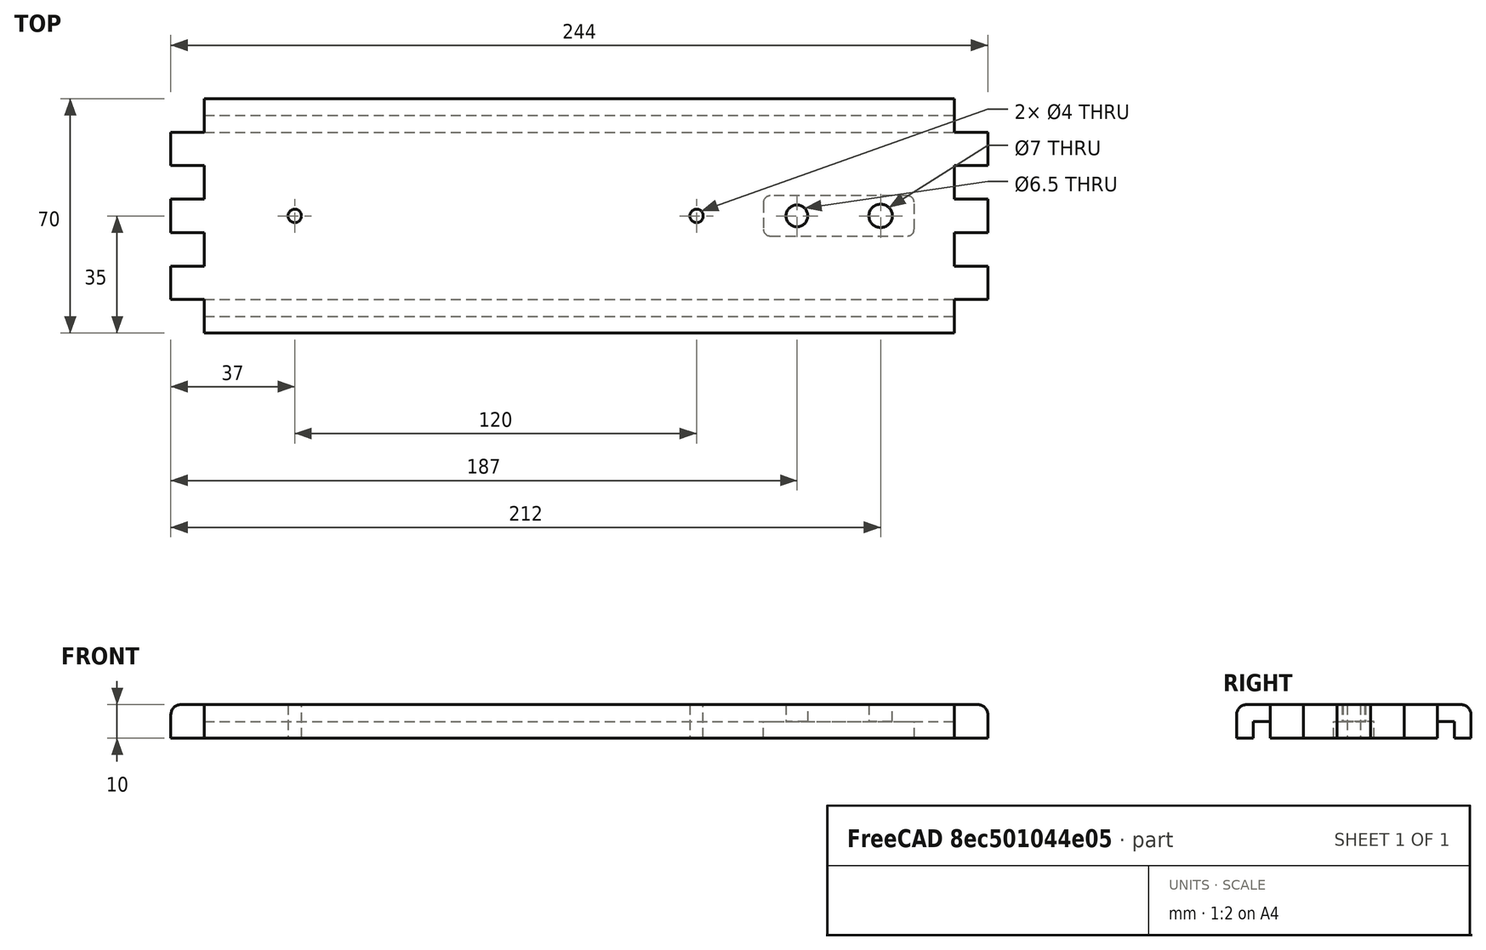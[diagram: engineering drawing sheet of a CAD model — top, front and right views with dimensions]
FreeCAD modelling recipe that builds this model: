
FCSTD DOCUMENT  (FreeCAD 0.18R16093 (Git))
Label: top
License: All rights reserved
LicenseURL: http://en.wikipedia.org/wiki/All_rights_reserved
objects: TechDraw::DrawViewDimension×15, PartDesign::Fillet×8, Sketcher::SketchObject×5, PartDesign::Pocket×4, TechDraw::DrawViewPart×3, PartDesign::Pad×1, PartDesign::Body×1, TechDraw::DrawSVGTemplate×1, TechDraw::DrawViewDetail×1, TechDraw::DrawViewSection×1, TechDraw::DrawPage×1, Drawing::FeatureViewPart×1, Drawing::FeaturePage×1
note: 24 computed .brp shape members not serialized (recipe doc carries the construction recipe); baked Part::Feature solids carry a one-line shape summary decoded from their .brp

FEATURE [Sketcher::SketchObject] Sketch
  MapMode = 5
  Support = -> [XY_Plane]
  sketch-geometry (4):
    g0: LineSegment StartX=-122 StartY=35 StartZ=0 EndX=122 EndY=35 EndZ=0
    g1: LineSegment StartX=122 StartY=35 StartZ=0 EndX=122 EndY=-35 EndZ=0
    g2: LineSegment StartX=122 StartY=-35 StartZ=0 EndX=-122 EndY=-35 EndZ=0
    g3: LineSegment StartX=-122 StartY=-35 StartZ=0 EndX=-122 EndY=35 EndZ=0
  constraints (10):
    c: DistanceX(g2,g1) = 244
    c: DistanceY(g1,g0) = 70
    c: Coincident(g2,g1)
    c: Coincident(g2,g3)
    c: Coincident(g3,g0)
    c: Coincident(g1,g0)
    c: Symmetric(g2,g1,g-2)
    c: Symmetric(g0,g1,g-1)
    c: Parallel(g0,g2)
    c: Parallel(g3,g1)
FEATURE [PartDesign::Pad] Pad
  Length = 10
  Length2 = 100
  Profile = -> Sketch
  Type = 0
FEATURE [PartDesign::Fillet] Fillet
  Base = -> Pad [Edge10]
  BaseFeature = -> Pad
  Radius = 3
FEATURE [PartDesign::Fillet] Fillet001
  Base = -> Fillet [Edge14]
  BaseFeature = -> Fillet
  Radius = 3
FEATURE [PartDesign::Fillet] Fillet002
  Base = -> Fillet001 [Edge19]
  BaseFeature = -> Fillet001
  Radius = 3
FEATURE [PartDesign::Fillet] Fillet003
  Base = -> Fillet002 [Edge1]
  BaseFeature = -> Fillet002
  Radius = 3
FEATURE [Sketcher::SketchObject] Sketch001
  MapMode = 5
  Placement = pos=(0,0,0) rot=(1,0,0;3.14159rad)
  Support = -> [Fillet003]
  sketch-geometry (8):
    g0: ArcOfCircle CenterX=-117 CenterY=27.5 CenterZ=0 NormalX=0 NormalY=0 NormalZ=1 AngleXU=0 Radius=2.5 StartAngle=1.5708 EndAngle=4.71239
    g1: ArcOfCircle CenterX=117 CenterY=27.5 CenterZ=0 NormalX=0 NormalY=0 NormalZ=1 AngleXU=0 Radius=2.5 StartAngle=4.71239 EndAngle=7.85398
    g2: LineSegment StartX=-117 StartY=25 StartZ=0 EndX=117 EndY=25 EndZ=0
    g3: LineSegment StartX=-117 StartY=30 StartZ=0 EndX=117 EndY=30 EndZ=0
    g4: ArcOfCircle CenterX=-117 CenterY=-27.5 CenterZ=0 NormalX=0 NormalY=0 NormalZ=1 AngleXU=0 Radius=2.5 StartAngle=1.5708 EndAngle=4.71239
    g5: ArcOfCircle CenterX=117 CenterY=-27.5 CenterZ=0 NormalX=0 NormalY=0 NormalZ=1 AngleXU=0 Radius=2.5 StartAngle=4.71239 EndAngle=7.85398
    g6: LineSegment StartX=-117 StartY=-30 StartZ=0 EndX=117 EndY=-30 EndZ=0
    g7: LineSegment StartX=-117 StartY=-25 StartZ=0 EndX=117 EndY=-25 EndZ=0
  constraints (19):
    c: Tangent(g0,g3) = 1.5708
    c: Tangent(g0,g2) = -1.5708
    c: Tangent(g2,g1) = -1.5708
    c: Tangent(g3,g1) = 1.5708
    c: Equal(g0,g1)
    c: Radius(g1) = 2.5
    c: Symmetric(g0,g1,g-2)
    c: DistanceX(g0,g1) = 234
    c: DistanceY(g-1,g0) = 25
    c: Tangent(g4,g7) = 1.5708
    c: Tangent(g4,g6) = -1.5708
    c: Tangent(g6,g5) = -1.5708
    c: Tangent(g7,g5) = 1.5708
    c: Horizontal(g6)
    c: Equal(g4,g5)
    c: Vertical(g4,g0)
    c: Vertical(g5,g1)
    c: Radius(g5) = 2.5
    c: DistanceY(g4,g-1) = 25
FEATURE [PartDesign::Pocket] Pocket
  BaseFeature = -> Fillet003
  Length = 5
  Length2 = 100
  Profile = -> Sketch001
  Type = 0
FEATURE [Sketcher::SketchObject] Sketch002
  MapMode = 5
  Placement = pos=(0,0,0) rot=(1,0,0;3.14159rad)
  Support = -> [Pocket]
  sketch-geometry (32):
    g0: LineSegment StartX=-122 StartY=15 StartZ=0 EndX=-112 EndY=15 EndZ=0
    g1: LineSegment StartX=-112 StartY=15 StartZ=0 EndX=-112 EndY=5 EndZ=0
    g2: LineSegment StartX=-112 StartY=5 StartZ=0 EndX=-122 EndY=5 EndZ=0
    g3: LineSegment StartX=-122 StartY=5 StartZ=0 EndX=-122 EndY=15 EndZ=0
    g4: LineSegment StartX=-122 StartY=35 StartZ=0 EndX=-112 EndY=35 EndZ=0
    g5: LineSegment StartX=-112 StartY=35 StartZ=0 EndX=-112 EndY=25 EndZ=0
    g6: LineSegment StartX=-112 StartY=25 StartZ=0 EndX=-122 EndY=25 EndZ=0
    g7: LineSegment StartX=-122 StartY=25 StartZ=0 EndX=-122 EndY=35 EndZ=0
    g8: LineSegment StartX=-122 StartY=-5 StartZ=0 EndX=-112 EndY=-5 EndZ=0
    g9: LineSegment StartX=-112 StartY=-5 StartZ=0 EndX=-112 EndY=-15 EndZ=0
    g10: LineSegment StartX=-112 StartY=-15 StartZ=0 EndX=-122 EndY=-15 EndZ=0
    g11: LineSegment StartX=-122 StartY=-15 StartZ=0 EndX=-122 EndY=-5 EndZ=0
    g12: LineSegment StartX=122 StartY=15 StartZ=0 EndX=112 EndY=15 EndZ=0
    g13: LineSegment StartX=112 StartY=15 StartZ=0 EndX=112 EndY=5 EndZ=0
    g14: LineSegment StartX=112 StartY=5 StartZ=0 EndX=122 EndY=5 EndZ=0
    g15: LineSegment StartX=122 StartY=5 StartZ=0 EndX=122 EndY=15 EndZ=0
    g16: LineSegment StartX=122 StartY=35 StartZ=0 EndX=112 EndY=35 EndZ=0
    g17: LineSegment StartX=112 StartY=35 StartZ=0 EndX=112 EndY=25 EndZ=0
    g18: LineSegment StartX=112 StartY=25 StartZ=0 EndX=122 EndY=25 EndZ=0
    g19: LineSegment StartX=122 StartY=25 StartZ=0 EndX=122 EndY=35 EndZ=0
    g20: LineSegment StartX=122 StartY=-5 StartZ=0 EndX=112 EndY=-5 EndZ=0
    g21: LineSegment StartX=112 StartY=-5 StartZ=0 EndX=112 EndY=-15 EndZ=0
    g22: LineSegment StartX=112 StartY=-15 StartZ=0 EndX=122 EndY=-15 EndZ=0
    g23: LineSegment StartX=122 StartY=-15 StartZ=0 EndX=122 EndY=-5 EndZ=0
    g24: LineSegment StartX=-122 StartY=-25 StartZ=0 EndX=-112 EndY=-25 EndZ=0
    g25: LineSegment StartX=-112 StartY=-25 StartZ=0 EndX=-112 EndY=-35 EndZ=0
    g26: LineSegment StartX=-112 StartY=-35 StartZ=0 EndX=-122 EndY=-35 EndZ=0
    g27: LineSegment StartX=-122 StartY=-35 StartZ=0 EndX=-122 EndY=-25 EndZ=0
    g28: LineSegment StartX=112 StartY=-25 StartZ=0 EndX=122 EndY=-25 EndZ=0
    g29: LineSegment StartX=122 StartY=-25 StartZ=0 EndX=122 EndY=-35 EndZ=0
    g30: LineSegment StartX=122 StartY=-35 StartZ=0 EndX=112 EndY=-35 EndZ=0
    g31: LineSegment StartX=112 StartY=-35 StartZ=0 EndX=112 EndY=-25 EndZ=0
  constraints (96):
    c: Coincident(g0,g1)
    c: Coincident(g1,g2)
    c: Coincident(g2,g3)
    c: Coincident(g3,g0)
    c: Horizontal(g0)
    c: Horizontal(g2)
    c: Vertical(g1)
    c: Vertical(g3)
    c: DistanceX(g2,g1) = 10
    c: DistanceY(g2,g0) = 10
    c: DistanceX(g1,g-1) = 112
    c: Coincident(g4,g5)
    c: Coincident(g6,g7)
    c: Coincident(g7,g4)
    c: Horizontal(g4)
    c: Horizontal(g6)
    c: Vertical(g5)
    c: Vertical(g7)
    c: Vertical(g5,g0)
    c: Vertical(g6,g0)
    c: DistanceY(g0,g6) = 10
    c: DistanceY(g6,g4) = 10
    c: Coincident(g8,g9)
    c: Coincident(g9,g10)
    c: Coincident(g10,g11)
    c: Coincident(g11,g8)
    c: Horizontal(g8)
    c: Horizontal(g10)
    c: Vertical(g9)
    c: Vertical(g11)
    c: Vertical(g8,g1)
    c: Vertical(g8,g2)
    c: DistanceY(g8,g2) = 10
    c: DistanceY(g10,g8) = 10
    c: Coincident(g12,g13)
    c: Coincident(g13,g14)
    c: Coincident(g14,g15)
    c: Coincident(g15,g12)
    c: Horizontal(g12)
    c: Horizontal(g14)
    c: Vertical(g13)
    c: Vertical(g15)
    c: Coincident(g16,g17)
    c: Coincident(g18,g19)
    c: Coincident(g19,g16)
    c: Horizontal(g16)
    c: Horizontal(g18)
    c: Vertical(g17)
    c: Vertical(g19)
    c: Coincident(g20,g21)
    c: Coincident(g21,g22)
    c: Coincident(g22,g23)
    c: Coincident(g23,g20)
    c: Horizontal(g20)
    c: Horizontal(g22)
    c: Vertical(g21)
    c: Vertical(g23)
    c: DistanceX(g-1,g12) = 112
    c: DistanceX(g12,g12) = 10
    c: Vertical(g12,g17)
    c: Vertical(g13,g20)
    c: Vertical(g20,g14)
    c: Vertical(g12,g18)
    c: Horizontal(g4,g16)
    c: Coincident(g24,g25)
    c: Coincident(g25,g26)
    c: Coincident(g26,g27)
    c: Coincident(g27,g24)
    c: Horizontal(g24)
    c: Horizontal(g26)
    c: Vertical(g25)
    c: Vertical(g27)
    c: Coincident(g28,g29)
    c: Coincident(g29,g30)
    c: Coincident(g30,g31)
    c: Coincident(g31,g28)
    c: Horizontal(g28)
    c: Horizontal(g30)
    c: Vertical(g29)
    c: Vertical(g31)
    c: Vertical(g24,g10)
    c: Vertical(g24,g9)
    c: Vertical(g28,g21)
    c: Vertical(g28,g22)
    c: DistanceY(g24,g9) = 10
    c: DistanceY(g25,g24) = 10
    c: Horizontal(g5,g17)
    c: Horizontal(g0,g12)
    c: Horizontal(g13,g1)
    c: Horizontal(g20,g8)
    c: Horizontal(g21,g9)
    c: Horizontal(g28,g24)
    c: Horizontal(g30,g25)
    c: DistanceY(g-1,g6) = 25
    c: Coincident(g6,g5)
    c: Coincident(g18,g17)
FEATURE [PartDesign::Pocket] Pocket001
  BaseFeature = -> Pocket
  Length = 5
  Length2 = 100
  Profile = -> Sketch002
  Type = 1
FEATURE [Sketcher::SketchObject] Sketch003
  MapMode = 5
  Placement = pos=(0,0,0) rot=(1,0,0;3.14159rad)
  Support = -> [Pocket001]
  sketch-geometry (4):
    g0: Circle CenterX=90 CenterY=0 CenterZ=0 NormalX=0 NormalY=0 NormalZ=1 AngleXU=0 Radius=3.5
    g1: Circle CenterX=65 CenterY=0 CenterZ=0 NormalX=0 NormalY=0 NormalZ=1 AngleXU=0 Radius=3.25
    g2: Circle CenterX=-85 CenterY=0 CenterZ=0 NormalX=0 NormalY=0 NormalZ=1 AngleXU=0 Radius=2
    g3: Circle CenterX=35 CenterY=0 CenterZ=0 NormalX=0 NormalY=0 NormalZ=1 AngleXU=0 Radius=2
  constraints (12):
    c: PointOnObject(g0,g-1)
    c: Radius(g0) = 3.5
    c: PointOnObject(g1,g-1)
    c: Radius(g1) = 3.25
    c: PointOnObject(g2,g-1)
    c: Radius(g2) = 2
    c: DistanceX(g-1,g0) = 90
    c: DistanceX(g1,g0) = 25
    c: DistanceX(g2,g3) = 120
    c: DistanceX(g2,g-1) = 85
    c: Radius(g3) = 2
    c: PointOnObject(g3,g-1)
FEATURE [PartDesign::Pocket] Pocket002
  BaseFeature = -> Pocket001
  Length = 5
  Length2 = 100
  Profile = -> Sketch003
  Type = 1
FEATURE [Sketcher::SketchObject] Sketch004
  MapMode = 5
  Placement = pos=(0,0,0) rot=(1,0,0;3.14159rad)
  Support = -> [Pocket002]
  sketch-geometry (4):
    g0: LineSegment StartX=55 StartY=6 StartZ=0 EndX=100 EndY=6 EndZ=0
    g1: LineSegment StartX=100 StartY=6 StartZ=0 EndX=100 EndY=-6 EndZ=0
    g2: LineSegment StartX=100 StartY=-6 StartZ=0 EndX=55 EndY=-6 EndZ=0
    g3: LineSegment StartX=55 StartY=-6 StartZ=0 EndX=55 EndY=6 EndZ=0
  constraints (10):
    c: Coincident(g0,g1)
    c: Coincident(g1,g2)
    c: Coincident(g2,g3)
    c: Coincident(g3,g0)
    c: Symmetric(g0,g2,g-1)
    c: DistanceY(g1,g0) = 12
    c: DistanceX(g-1,g1) = 100
    c: DistanceX(g0,g0) = 45
    c: Symmetric(g1,g0,g-1)
    c: Parallel(g0,g2)
FEATURE [PartDesign::Pocket] Pocket003
  BaseFeature = -> Pocket002
  Length = 5
  Length2 = 100
  Profile = -> Sketch004
  Type = 0
FEATURE [PartDesign::Fillet] Fillet004
  Base = -> Pocket003 [Edge113]
  BaseFeature = -> Pocket003
  Radius = 2
FEATURE [PartDesign::Fillet] Fillet005
  Base = -> Fillet004 [Edge37]
  BaseFeature = -> Fillet004
  Radius = 2
FEATURE [PartDesign::Fillet] Fillet006
  Base = -> Fillet005 [Edge44]
  BaseFeature = -> Fillet005
  Radius = 2
FEATURE [PartDesign::Fillet] Fillet007
  Base = -> Fillet006 [Edge45]
  BaseFeature = -> Fillet006
  Radius = 2
FEATURE [PartDesign::Body] Body  label="topPlate"
  Group = -> [Sketch,Pad,Fillet,Fillet001,Fillet002,Fillet003,Sketch001,Pocket,Sketch002,Pocket001,Sketch003,Pocket002,Sketch004,Pocket003,Fillet004,Fillet005,Fillet006,Fillet007]
  Origin = -> Origin
  Placement = pos=(140,-80,0) rot=(0,0,1;0rad)
  Tip = -> Fillet007
FEATURE [TechDraw::DrawSVGTemplate] Template
  EditableTexts = Designed_by_Name=Andreas Renggli; Drawing_number=-; FC-Date=07.12.2018; FC-SC=1:2; FC-SH=1; FC-Title=MusicBox; Subtitle=TopPlate; Weight=-
  Height = 210
  Orientation = 1
  Width = 297
FEATURE [TechDraw::DrawViewPart] View
  CoarseView = false
  Direction = (0,0,-1)
  Focus = 100
  HardHidden = false
  IsoCount = 0
  IsoHidden = false
  IsoVisible = false
  LockPosition = false
  Perspective = false
  Rotation = 0
  Scale = 0.5
  ScaleType = 2
  SeamHidden = false
  SeamVisible = false
  SmoothHidden = false
  SmoothVisible = false
  Source = -> [Body]
  X = 200.699
  Y = 159.162
FEATURE [TechDraw::DrawViewDimension] Dimension
  Arbitrary = false
  FormatSpec = %.2f
  LockPosition = false
  MeasureType = 1
  OverTolerance = 0
  References2D = -> [View]
  Rotation = 0
  ScaleType = 0
  Type = 1
  UnderTolerance = 0
  X = 2.05346
  Y = -56
FEATURE [TechDraw::DrawViewDimension] Dimension001
  Arbitrary = false
  FormatSpec = %.2f
  LockPosition = false
  MeasureType = 1
  OverTolerance = 0
  References2D = -> [View]
  Rotation = 0
  ScaleType = 0
  Type = 2
  UnderTolerance = 0
  X = -86.4429
  Y = 2.33067
FEATURE [TechDraw::DrawViewDimension] Dimension002
  Arbitrary = false
  FormatSpec = %.2f
  LockPosition = false
  MeasureType = 1
  OverTolerance = 0
  References2D = -> [View]
  Rotation = 0
  ScaleType = 0
  Type = 1
  UnderTolerance = 0
  X = -29.0825
  Y = -28
FEATURE [TechDraw::DrawViewDimension] Dimension003
  Arbitrary = false
  FormatSpec = %.2f
  LockPosition = false
  MeasureType = 1
  OverTolerance = 0
  References2D = -> [View]
  Rotation = 0
  ScaleType = 0
  Type = 1
  UnderTolerance = 0
  X = -20.7483
  Y = -35
FEATURE [TechDraw::DrawViewDimension] Dimension004
  Arbitrary = false
  FormatSpec = %.2f
  LockPosition = false
  MeasureType = 1
  OverTolerance = 0
  References2D = -> [View]
  Rotation = 0
  ScaleType = 0
  Type = 1
  UnderTolerance = 0
  X = -16
  Y = -41
FEATURE [TechDraw::DrawViewDimension] Dimension005
  Arbitrary = false
  FormatSpec = %.2f
  LockPosition = false
  MeasureType = 1
  OverTolerance = 0
  References2D = -> [View]
  Rotation = 0
  ScaleType = 0
  Type = 1
  UnderTolerance = 0
  X = -5.9697
  Y = -49
FEATURE [TechDraw::DrawViewDimension] Dimension006
  Arbitrary = false
  FormatSpec = %.2f
  LockPosition = false
  MeasureType = 1
  OverTolerance = 0
  References2D = -> [View]
  Rotation = 0
  ScaleType = 0
  Type = 2
  UnderTolerance = 0
  X = -74.082
  Y = -3.12143
FEATURE [TechDraw::DrawViewDimension] Dimension007
  Arbitrary = false
  FormatSpec = %.2f
  LockPosition = false
  MeasureType = 1
  OverTolerance = 0
  References2D = -> [View]
  Rotation = 0
  ScaleType = 0
  Type = 5
  UnderTolerance = 0
  X = -14.2913
  Y = 28.4727
FEATURE [TechDraw::DrawViewDimension] Dimension008
  Arbitrary = false
  FormatSpec = %.2f
  LockPosition = false
  MeasureType = 1
  OverTolerance = 0
  References2D = -> [View]
  Rotation = 0
  ScaleType = 0
  Type = 5
  UnderTolerance = 0
  X = 50.6791
  Y = 32.7601
FEATURE [TechDraw::DrawViewDimension] Dimension009
  Arbitrary = false
  FormatSpec = %.2f
  LockPosition = false
  MeasureType = 1
  OverTolerance = 0
  References2D = -> [View]
  Rotation = 0
  ScaleType = 0
  Type = 5
  UnderTolerance = 0
  X = 65.1903
  Y = 25.8343
FEATURE [TechDraw::DrawViewDimension] Dimension010
  Arbitrary = false
  FormatSpec = %.2f
  LockPosition = false
  MeasureType = 1
  OverTolerance = 0
  References2D = -> [View]
  Rotation = 0
  ScaleType = 0
  Type = 5
  UnderTolerance = 0
  X = 73.985
  Y = 20.8873
FEATURE [TechDraw::DrawViewDetail] Detail
  AnchorPoint = (60,0,0)
  BaseView = -> View
  CoarseView = false
  Direction = (0,0,-1)
  Focus = 100
  HardHidden = false
  IsoCount = 0
  IsoHidden = false
  IsoVisible = false
  LockPosition = false
  Perspective = false
  Radius = 10
  Reference = 1
  Rotation = 0
  ScaleType = 0
  SeamHidden = false
  SeamVisible = false
  SmoothHidden = false
  SmoothVisible = false
  Source = -> [Body]
  X = 252.034
  Y = 76.4572
FEATURE [TechDraw::DrawViewDimension] Dimension011
  Arbitrary = false
  FormatSpec = %.2f
  LockPosition = false
  MeasureType = 1
  OverTolerance = 0
  References2D = -> [Detail]
  Rotation = 0
  ScaleType = 0
  Type = 4
  UnderTolerance = 0
  X = 7.59857
  Y = 18.0466
FEATURE [TechDraw::DrawViewSection] Section  label="Section A - A"
  BaseView = -> View
  CoarseView = false
  Direction = (-1,0,0)
  Focus = 100
  FuseBeforeCut = true
  HardHidden = false
  HatchScale = 1
  IsoCount = 0
  IsoHidden = false
  IsoVisible = false
  LockPosition = false
  NameGeomPattern = Diamond
  Perspective = false
  Rotation = 0
  Scale = 0.5
  ScaleType = 2
  SeamHidden = false
  SeamVisible = false
  SectionDirection = 0
  SectionNormal = (-1,0,0)
  SectionOrigin = (130,-80,5)
  SectionSymbol = A
  SmoothHidden = false
  SmoothVisible = false
  Source = -> [Body]
  X = 47.2828
  Y = 177.405
FEATURE [TechDraw::DrawViewDimension] Dimension012
  Arbitrary = false
  FormatSpec = %.2f
  LockPosition = false
  MeasureType = 1
  OverTolerance = 0
  References2D = -> [Section]
  Rotation = 0
  ScaleType = 0
  Type = 2
  UnderTolerance = 0
  X = 26.842
  Y = 9.34431
FEATURE [TechDraw::DrawViewDimension] Dimension013
  Arbitrary = false
  FormatSpec = %.2f
  LockPosition = false
  MeasureType = 1
  OverTolerance = 0
  References2D = -> [Section]
  Rotation = 0
  ScaleType = 0
  Type = 2
  UnderTolerance = 0
  X = 39.9423
  Y = 12.0926
FEATURE [TechDraw::DrawViewDimension] Dimension019
  Arbitrary = false
  FormatSpec = %.2f
  LockPosition = false
  MeasureType = 1
  OverTolerance = 0
  References2D = -> [View]
  Rotation = 0
  ScaleType = 0
  Type = 1
  UnderTolerance = 0
  X = -44.2203
  Y = -22
FEATURE [TechDraw::DrawViewPart] View001
  CoarseView = false
  Direction = (-1,-1,1)
  Focus = 100
  HardHidden = false
  IsoCount = 0
  IsoHidden = false
  IsoVisible = false
  LockPosition = false
  Perspective = false
  Rotation = 0
  Scale = 0.5
  ScaleType = 2
  SeamHidden = false
  SeamVisible = false
  SmoothHidden = false
  SmoothVisible = false
  Source = -> [Body]
  X = 80
  Y = 86
FEATURE [TechDraw::DrawViewPart] View002
  CoarseView = false
  Direction = (-1,1,-1)
  Focus = 100
  HardHidden = false
  IsoCount = 0
  IsoHidden = false
  IsoVisible = false
  LockPosition = false
  Perspective = false
  Rotation = 180
  Scale = 0.5
  ScaleType = 2
  SeamHidden = false
  SeamVisible = false
  SmoothHidden = false
  SmoothVisible = false
  Source = -> [Body]
  X = 80
  Y = 45
FEATURE [TechDraw::DrawPage] Page
  KeepUpdated = true
  ProjectionType = 0
  Template = -> Template
  Views = -> [View,Dimension,Dimension001,Dimension002,Dimension003,Dimension004,Dimension005,Dimension006,Dimension007,Dimension008,Dimension009,Dimension010,Detail,Dimension011,Section,Dimension012,Dimension013,Dimension019,View001,View002]
FEATURE [Drawing::FeatureViewPart] View003
  Direction = (0,0,1)
  HiddenWidth = 0.15
  LineWidth = 0.1
  Rotation = 0
  ShowHiddenLines = false
  ShowSmoothLines = false
  Source = -> Body
  Tolerance = 0.05
  ViewResult = <blob: 7351 chars omitted>
  Visible = false
  X = 10
  Y = 10
FEATURE [Drawing::FeaturePage] Page001
  EditableTexts = AUTHOR NAME | DRAWING TITLE | FreeCAD DRAWING | A4 | X / Y | SCALE | PN | DN | DD/MM/YYYY | REV A
  Group = -> [View003]
  Template = <path>
note: 1 file-system path scrubbed to <path> (originals preserved in the JSON sidecar)
